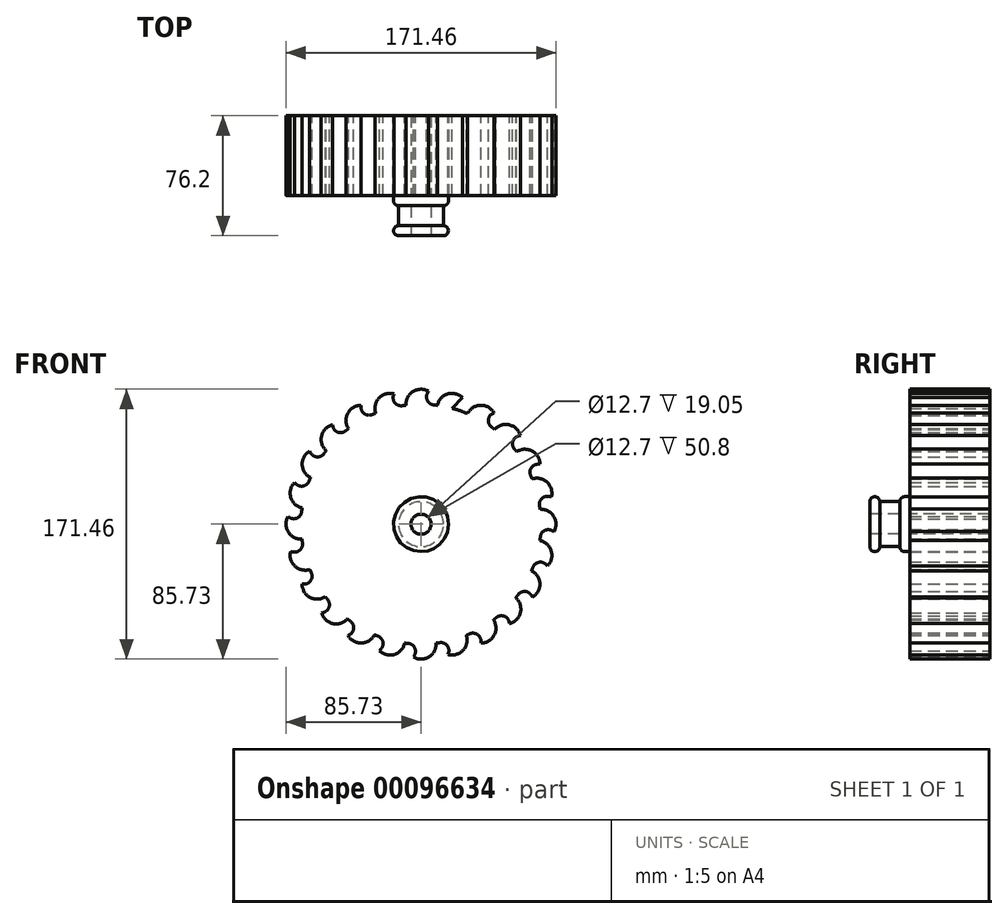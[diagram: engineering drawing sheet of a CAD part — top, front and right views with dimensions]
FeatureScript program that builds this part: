
annotation { "Feature Type Name" : "Feature", "Feature Type Description" : "" }
export const myFeature = defineFeature(function(context is Context, id is Id, definition is map)
    precondition{}
    {
        {
            var Q0;
            Q0=qCreatedBy(makeId("Front.planeOp"),FACE);
            var sketch = newSketch(context, id + "F0", { "sketchPlane" : qUnion([Q0])});
            skArc(sketch, "E0", {"start": v(-9.5, 75.6) * mm, "mid": v(-14.65, 74.78) * mm, "end": v(-19.72, 73.6) * mm});
            skLineSegment(sketch, "E1", {"start": v(0, 76.2) * mm, "end": v(0, 0) * mm, "construction": true});
            skArc(sketch, "E2", {"start": v(4.76, 84.45) * mm, "mid": v(-5.02, 84.3) * mm, "end": v(-9.5, 75.6) * mm});
            skLineSegment(sketch, "E3", {"start": v(0, 76.2) * mm, "end": v(4.76, 84.45) * mm});
            skLineSegment(sketch, "E4", {"start": v(0, 0) * mm, "end": v(82.95, 0) * mm, "construction": true});
            skArc(sketch, "E5.1.0", {"start": v(-17.26, 82.8) * mm, "mid": v(-26.66, 80.12) * mm, "end": v(-28.75, 70.57) * mm});
            skArc(sketch, "E5.2.0", {"start": v(-38.1, 75.52) * mm, "mid": v(-46.5, 70.5) * mm, "end": v(-46.04, 60.72) * mm});
            skArc(sketch, "E5.3.0", {"start": v(-56.35, 63.08) * mm, "mid": v(-63.15, 56.06) * mm, "end": v(-60.18, 46.74) * mm});
            skArc(sketch, "E5.4.0", {"start": v(-70.75, 46.35) * mm, "mid": v(-75.51, 37.8) * mm, "end": v(-70.23, 29.57) * mm});
            skArc(sketch, "E5.5.0", {"start": v(-80.34, 26.46) * mm, "mid": v(-82.72, 16.97) * mm, "end": v(-75.49, 10.39) * mm});
            skArc(sketch, "E5.6.0", {"start": v(-84.45, 4.76) * mm, "mid": v(-84.3, -5.02) * mm, "end": v(-75.6, -9.5) * mm});
            skArc(sketch, "E5.7.0", {"start": v(-82.8, -17.26) * mm, "mid": v(-80.12, -26.66) * mm, "end": v(-70.57, -28.75) * mm});
            skArc(sketch, "E5.8.0", {"start": v(-75.52, -38.1) * mm, "mid": v(-70.5, -46.5) * mm, "end": v(-60.72, -46.04) * mm});
            skArc(sketch, "E5.9.0", {"start": v(-63.08, -56.35) * mm, "mid": v(-56.06, -63.15) * mm, "end": v(-46.74, -60.18) * mm});
            skArc(sketch, "E5.10.0", {"start": v(-46.35, -70.75) * mm, "mid": v(-37.8, -75.51) * mm, "end": v(-29.57, -70.23) * mm});
            skArc(sketch, "E5.11.0", {"start": v(-26.46, -80.34) * mm, "mid": v(-16.97, -82.72) * mm, "end": v(-10.39, -75.49) * mm});
            skArc(sketch, "E5.12.0", {"start": v(-4.76, -84.45) * mm, "mid": v(5.02, -84.3) * mm, "end": v(9.5, -75.6) * mm});
            skArc(sketch, "E5.13.0", {"start": v(17.26, -82.8) * mm, "mid": v(26.66, -80.12) * mm, "end": v(28.75, -70.57) * mm});
            skArc(sketch, "E5.14.0", {"start": v(38.1, -75.52) * mm, "mid": v(46.5, -70.5) * mm, "end": v(46.04, -60.72) * mm});
            skArc(sketch, "E5.15.0", {"start": v(56.35, -63.08) * mm, "mid": v(63.15, -56.06) * mm, "end": v(60.18, -46.74) * mm});
            skArc(sketch, "E5.16.0", {"start": v(70.75, -46.35) * mm, "mid": v(75.51, -37.8) * mm, "end": v(70.23, -29.57) * mm});
            skArc(sketch, "E5.17.0", {"start": v(80.34, -26.46) * mm, "mid": v(82.72, -16.97) * mm, "end": v(75.49, -10.39) * mm});
            skArc(sketch, "E5.18.0", {"start": v(84.45, -4.76) * mm, "mid": v(84.3, 5.02) * mm, "end": v(75.6, 9.5) * mm});
            skArc(sketch, "E5.19.0", {"start": v(82.8, 17.26) * mm, "mid": v(80.12, 26.66) * mm, "end": v(70.57, 28.75) * mm});
            skArc(sketch, "E5.20.0", {"start": v(75.52, 38.1) * mm, "mid": v(70.5, 46.5) * mm, "end": v(60.72, 46.04) * mm});
            skArc(sketch, "E5.21.0", {"start": v(63.08, 56.35) * mm, "mid": v(56.06, 63.15) * mm, "end": v(46.74, 60.18) * mm});
            skArc(sketch, "E5.22.0", {"start": v(46.35, 70.75) * mm, "mid": v(37.8, 75.51) * mm, "end": v(29.57, 70.23) * mm});
            skArc(sketch, "E5.23.0", {"start": v(26.46, 80.34) * mm, "mid": v(16.97, 82.72) * mm, "end": v(10.39, 75.49) * mm});
            skLineSegment(sketch, "E6.1.0", {"start": v(-19.72, 73.6) * mm, "end": v(-17.26, 82.8) * mm});
            skLineSegment(sketch, "E6.2.0", {"start": v(-38.1, 66) * mm, "end": v(-38.1, 75.52) * mm});
            skLineSegment(sketch, "E6.3.0", {"start": v(-53.88, 53.88) * mm, "end": v(-56.35, 63.08) * mm});
            skLineSegment(sketch, "E6.4.0", {"start": v(-66, 38.1) * mm, "end": v(-70.75, 46.35) * mm});
            skLineSegment(sketch, "E6.5.0", {"start": v(-73.6, 19.72) * mm, "end": v(-80.34, 26.46) * mm});
            skLineSegment(sketch, "E6.6.0", {"start": v(-76.2, 0) * mm, "end": v(-84.45, 4.76) * mm});
            skLineSegment(sketch, "E6.7.0", {"start": v(-73.6, -19.72) * mm, "end": v(-82.8, -17.26) * mm});
            skLineSegment(sketch, "E6.8.0", {"start": v(-66, -38.1) * mm, "end": v(-75.52, -38.1) * mm});
            skLineSegment(sketch, "E6.9.0", {"start": v(-53.88, -53.88) * mm, "end": v(-63.08, -56.35) * mm});
            skLineSegment(sketch, "E6.10.0", {"start": v(-38.1, -66) * mm, "end": v(-46.35, -70.75) * mm});
            skLineSegment(sketch, "E6.11.0", {"start": v(-19.72, -73.6) * mm, "end": v(-26.46, -80.34) * mm});
            skLineSegment(sketch, "E6.12.0", {"start": v(0, -76.2) * mm, "end": v(-4.76, -84.45) * mm});
            skLineSegment(sketch, "E6.13.0", {"start": v(19.72, -73.6) * mm, "end": v(17.26, -82.8) * mm});
            skLineSegment(sketch, "E6.14.0", {"start": v(38.1, -66) * mm, "end": v(38.1, -75.52) * mm});
            skLineSegment(sketch, "E6.15.0", {"start": v(53.88, -53.88) * mm, "end": v(56.35, -63.08) * mm});
            skLineSegment(sketch, "E6.16.0", {"start": v(66, -38.1) * mm, "end": v(70.75, -46.35) * mm});
            skLineSegment(sketch, "E6.17.0", {"start": v(73.6, -19.72) * mm, "end": v(80.34, -26.46) * mm});
            skLineSegment(sketch, "E6.18.0", {"start": v(76.2, 0) * mm, "end": v(84.45, -4.76) * mm});
            skLineSegment(sketch, "E6.19.0", {"start": v(73.6, 19.72) * mm, "end": v(82.8, 17.26) * mm});
            skLineSegment(sketch, "E6.20.0", {"start": v(66, 38.1) * mm, "end": v(75.52, 38.1) * mm});
            skLineSegment(sketch, "E6.21.0", {"start": v(53.88, 53.88) * mm, "end": v(63.08, 56.35) * mm});
            skLineSegment(sketch, "E6.22.0", {"start": v(38.1, 66) * mm, "end": v(46.35, 70.75) * mm});
            skLineSegment(sketch, "E6.23.0", {"start": v(19.72, 73.6) * mm, "end": v(26.46, 80.34) * mm});
            skArc(sketch, "E7.trimOffspring", {"start": v(-46.04, 60.72) * mm, "mid": v(-50.08, 57.44) * mm, "end": v(-53.88, 53.88) * mm});
            skArc(sketch, "E8.trimOffspring", {"start": v(-28.75, 70.57) * mm, "mid": v(-33.5, 68.44) * mm, "end": v(-38.1, 66) * mm});
            skArc(sketch, "E9.trimOffspring", {"start": v(-60.18, 46.74) * mm, "mid": v(-63.23, 42.52) * mm, "end": v(-66, 38.1) * mm});
            skArc(sketch, "E10.trimOffspring", {"start": v(10.39, 75.49) * mm, "mid": v(5.2, 76.02) * mm, "end": v(0, 76.2) * mm});
            skArc(sketch, "E11.trimOffspring", {"start": v(29.57, 70.23) * mm, "mid": v(24.7, 72.08) * mm, "end": v(19.72, 73.6) * mm});
            skArc(sketch, "E12.trimOffspring", {"start": v(46.74, 60.18) * mm, "mid": v(42.52, 63.23) * mm, "end": v(38.1, 66) * mm});
            skArc(sketch, "E13.trimOffspring", {"start": v(60.72, 46.04) * mm, "mid": v(57.44, 50.08) * mm, "end": v(53.88, 53.88) * mm});
            skArc(sketch, "E14.trimOffspring", {"start": v(70.57, 28.75) * mm, "mid": v(68.44, 33.5) * mm, "end": v(66, 38.1) * mm});
            skArc(sketch, "E15.trimOffspring", {"start": v(75.6, 9.5) * mm, "mid": v(74.78, 14.65) * mm, "end": v(73.6, 19.72) * mm});
            skArc(sketch, "E16.trimOffspring", {"start": v(75.49, -10.39) * mm, "mid": v(76.02, -5.2) * mm, "end": v(76.2, 0) * mm});
            skArc(sketch, "E17.trimOffspring", {"start": v(70.23, -29.57) * mm, "mid": v(72.08, -24.7) * mm, "end": v(73.6, -19.72) * mm});
            skArc(sketch, "E18.trimOffspring", {"start": v(60.18, -46.74) * mm, "mid": v(63.23, -42.52) * mm, "end": v(66, -38.1) * mm});
            skArc(sketch, "E19.trimOffspring", {"start": v(46.04, -60.72) * mm, "mid": v(50.08, -57.44) * mm, "end": v(53.88, -53.88) * mm});
            skArc(sketch, "E20.trimOffspring", {"start": v(28.75, -70.57) * mm, "mid": v(33.5, -68.44) * mm, "end": v(38.1, -66) * mm});
            skArc(sketch, "E21.trimOffspring", {"start": v(9.5, -75.6) * mm, "mid": v(14.65, -74.78) * mm, "end": v(19.72, -73.6) * mm});
            skArc(sketch, "E22.trimOffspring", {"start": v(-10.39, -75.49) * mm, "mid": v(-5.2, -76.02) * mm, "end": v(0, -76.2) * mm});
            skArc(sketch, "E23.trimOffspring", {"start": v(-29.57, -70.23) * mm, "mid": v(-24.7, -72.08) * mm, "end": v(-19.72, -73.6) * mm});
            skArc(sketch, "E24.trimOffspring", {"start": v(-46.74, -60.18) * mm, "mid": v(-42.52, -63.23) * mm, "end": v(-38.1, -66) * mm});
            skArc(sketch, "E25.trimOffspring", {"start": v(-60.72, -46.04) * mm, "mid": v(-57.44, -50.08) * mm, "end": v(-53.88, -53.88) * mm});
            skArc(sketch, "E26.trimOffspring", {"start": v(-70.57, -28.75) * mm, "mid": v(-68.44, -33.5) * mm, "end": v(-66, -38.1) * mm});
            skArc(sketch, "E27.trimOffspring", {"start": v(-75.6, -9.5) * mm, "mid": v(-74.78, -14.65) * mm, "end": v(-73.6, -19.72) * mm});
            skArc(sketch, "E28.trimOffspring", {"start": v(-75.49, 10.39) * mm, "mid": v(-76.02, 5.2) * mm, "end": v(-76.2, 0) * mm});
            skArc(sketch, "E29.trimOffspring", {"start": v(-70.23, 29.57) * mm, "mid": v(-72.08, 24.7) * mm, "end": v(-73.6, 19.72) * mm});
            skSolve(sketch);
        }
        {
            var Q0;
            Q0=makeQuery(id+"F0.imprint","IMPRINT",FACE,{"disambiguationData":[TD([[makeQuery(id+"F0.imprint","IMPRINT",EDGE,{"derivedFrom":sQuery(id+"F0.wireOp",EDGE,"E0")}),1.0]])]});
            extrude(context, id + "F1", {"entities" : qUnion([Q0]), "depth" : 50.8 * mm});
        }
        {
            var Q0;
            Q0=makeQuery(id+"F1.opExtrude","CAP_FACE",FACE,{"disambiguationData":[OSD([sQuery(id+"F0.wireOp",EDGE,"E0"),sQuery(id+"F0.wireOp",EDGE,"E2"),sQuery(id+"F0.wireOp",EDGE,"E3"),sQuery(id+"F0.wireOp",EDGE,"E5.1.0"),sQuery(id+"F0.wireOp",EDGE,"E5.2.0"),sQuery(id+"F0.wireOp",EDGE,"E5.3.0"),sQuery(id+"F0.wireOp",EDGE,"E5.4.0"),sQuery(id+"F0.wireOp",EDGE,"E5.5.0"),sQuery(id+"F0.wireOp",EDGE,"E5.6.0"),sQuery(id+"F0.wireOp",EDGE,"E5.7.0"),sQuery(id+"F0.wireOp",EDGE,"E5.8.0"),sQuery(id+"F0.wireOp",EDGE,"E5.9.0"),sQuery(id+"F0.wireOp",EDGE,"E5.10.0"),sQuery(id+"F0.wireOp",EDGE,"E5.11.0"),sQuery(id+"F0.wireOp",EDGE,"E5.12.0"),sQuery(id+"F0.wireOp",EDGE,"E5.13.0"),sQuery(id+"F0.wireOp",EDGE,"E5.14.0"),sQuery(id+"F0.wireOp",EDGE,"E5.15.0"),sQuery(id+"F0.wireOp",EDGE,"E5.16.0"),sQuery(id+"F0.wireOp",EDGE,"E5.17.0"),sQuery(id+"F0.wireOp",EDGE,"E5.18.0"),sQuery(id+"F0.wireOp",EDGE,"E5.19.0"),sQuery(id+"F0.wireOp",EDGE,"E5.20.0"),sQuery(id+"F0.wireOp",EDGE,"E5.21.0"),sQuery(id+"F0.wireOp",EDGE,"E5.22.0"),sQuery(id+"F0.wireOp",EDGE,"E5.23.0"),sQuery(id+"F0.wireOp",EDGE,"E6.1.0"),sQuery(id+"F0.wireOp",EDGE,"E6.2.0"),sQuery(id+"F0.wireOp",EDGE,"E6.3.0"),sQuery(id+"F0.wireOp",EDGE,"E6.4.0"),sQuery(id+"F0.wireOp",EDGE,"E6.5.0"),sQuery(id+"F0.wireOp",EDGE,"E6.6.0"),sQuery(id+"F0.wireOp",EDGE,"E6.7.0"),sQuery(id+"F0.wireOp",EDGE,"E6.8.0"),sQuery(id+"F0.wireOp",EDGE,"E6.9.0"),sQuery(id+"F0.wireOp",EDGE,"E6.10.0"),sQuery(id+"F0.wireOp",EDGE,"E6.11.0"),sQuery(id+"F0.wireOp",EDGE,"E6.12.0"),sQuery(id+"F0.wireOp",EDGE,"E6.13.0"),sQuery(id+"F0.wireOp",EDGE,"E6.14.0"),sQuery(id+"F0.wireOp",EDGE,"E6.15.0"),sQuery(id+"F0.wireOp",EDGE,"E6.16.0"),sQuery(id+"F0.wireOp",EDGE,"E6.17.0"),sQuery(id+"F0.wireOp",EDGE,"E6.18.0"),sQuery(id+"F0.wireOp",EDGE,"E6.19.0"),sQuery(id+"F0.wireOp",EDGE,"E6.20.0"),sQuery(id+"F0.wireOp",EDGE,"E6.21.0"),sQuery(id+"F0.wireOp",EDGE,"E6.22.0"),sQuery(id+"F0.wireOp",EDGE,"E6.23.0"),sQuery(id+"F0.wireOp",EDGE,"E7.trimOffspring"),sQuery(id+"F0.wireOp",EDGE,"E8.trimOffspring"),sQuery(id+"F0.wireOp",EDGE,"E9.trimOffspring"),sQuery(id+"F0.wireOp",EDGE,"E10.trimOffspring"),sQuery(id+"F0.wireOp",EDGE,"E11.trimOffspring"),sQuery(id+"F0.wireOp",EDGE,"E12.trimOffspring"),sQuery(id+"F0.wireOp",EDGE,"E13.trimOffspring"),sQuery(id+"F0.wireOp",EDGE,"E14.trimOffspring"),sQuery(id+"F0.wireOp",EDGE,"E15.trimOffspring"),sQuery(id+"F0.wireOp",EDGE,"E16.trimOffspring"),sQuery(id+"F0.wireOp",EDGE,"E17.trimOffspring"),sQuery(id+"F0.wireOp",EDGE,"E18.trimOffspring"),sQuery(id+"F0.wireOp",EDGE,"E19.trimOffspring"),sQuery(id+"F0.wireOp",EDGE,"E20.trimOffspring"),sQuery(id+"F0.wireOp",EDGE,"E21.trimOffspring"),sQuery(id+"F0.wireOp",EDGE,"E22.trimOffspring"),sQuery(id+"F0.wireOp",EDGE,"E23.trimOffspring"),sQuery(id+"F0.wireOp",EDGE,"E24.trimOffspring"),sQuery(id+"F0.wireOp",EDGE,"E25.trimOffspring"),sQuery(id+"F0.wireOp",EDGE,"E26.trimOffspring"),sQuery(id+"F0.wireOp",EDGE,"E27.trimOffspring"),sQuery(id+"F0.wireOp",EDGE,"E28.trimOffspring"),sQuery(id+"F0.wireOp",EDGE,"E29.trimOffspring")])],"isStart":false});
            var sketch = newSketch(context, id + "F2", { "sketchPlane" : qUnion([Q0])});
            skPoint(sketch, "E30", {"position": v(0, 0) * mm});
            skSolve(sketch);
        }
        {
            var Q0;
            Q0=sQuery(id+"F2.wireOp",VERTEX,"E30");
            var Q1;
            Q1=makeQuery(id+"F1.opExtrude","SWEPT_BODY",BODY,{"disambiguationData":[OSD([sQuery(id+"F0.wireOp",EDGE,"E0"),sQuery(id+"F0.wireOp",EDGE,"E2"),sQuery(id+"F0.wireOp",EDGE,"E3"),sQuery(id+"F0.wireOp",EDGE,"E5.1.0"),sQuery(id+"F0.wireOp",EDGE,"E5.2.0"),sQuery(id+"F0.wireOp",EDGE,"E5.3.0"),sQuery(id+"F0.wireOp",EDGE,"E5.4.0"),sQuery(id+"F0.wireOp",EDGE,"E5.5.0"),sQuery(id+"F0.wireOp",EDGE,"E5.6.0"),sQuery(id+"F0.wireOp",EDGE,"E5.7.0"),sQuery(id+"F0.wireOp",EDGE,"E5.8.0"),sQuery(id+"F0.wireOp",EDGE,"E5.9.0"),sQuery(id+"F0.wireOp",EDGE,"E5.10.0"),sQuery(id+"F0.wireOp",EDGE,"E5.11.0"),sQuery(id+"F0.wireOp",EDGE,"E5.12.0"),sQuery(id+"F0.wireOp",EDGE,"E5.13.0"),sQuery(id+"F0.wireOp",EDGE,"E5.14.0"),sQuery(id+"F0.wireOp",EDGE,"E5.15.0"),sQuery(id+"F0.wireOp",EDGE,"E5.16.0"),sQuery(id+"F0.wireOp",EDGE,"E5.17.0"),sQuery(id+"F0.wireOp",EDGE,"E5.18.0"),sQuery(id+"F0.wireOp",EDGE,"E5.19.0"),sQuery(id+"F0.wireOp",EDGE,"E5.20.0"),sQuery(id+"F0.wireOp",EDGE,"E5.21.0"),sQuery(id+"F0.wireOp",EDGE,"E5.22.0"),sQuery(id+"F0.wireOp",EDGE,"E5.23.0"),sQuery(id+"F0.wireOp",EDGE,"E6.1.0"),sQuery(id+"F0.wireOp",EDGE,"E6.2.0"),sQuery(id+"F0.wireOp",EDGE,"E6.3.0"),sQuery(id+"F0.wireOp",EDGE,"E6.4.0"),sQuery(id+"F0.wireOp",EDGE,"E6.5.0"),sQuery(id+"F0.wireOp",EDGE,"E6.6.0"),sQuery(id+"F0.wireOp",EDGE,"E6.7.0"),sQuery(id+"F0.wireOp",EDGE,"E6.8.0"),sQuery(id+"F0.wireOp",EDGE,"E6.9.0"),sQuery(id+"F0.wireOp",EDGE,"E6.10.0"),sQuery(id+"F0.wireOp",EDGE,"E6.11.0"),sQuery(id+"F0.wireOp",EDGE,"E6.12.0"),sQuery(id+"F0.wireOp",EDGE,"E6.13.0"),sQuery(id+"F0.wireOp",EDGE,"E6.14.0"),sQuery(id+"F0.wireOp",EDGE,"E6.15.0"),sQuery(id+"F0.wireOp",EDGE,"E6.16.0"),sQuery(id+"F0.wireOp",EDGE,"E6.17.0"),sQuery(id+"F0.wireOp",EDGE,"E6.18.0"),sQuery(id+"F0.wireOp",EDGE,"E6.19.0"),sQuery(id+"F0.wireOp",EDGE,"E6.20.0"),sQuery(id+"F0.wireOp",EDGE,"E6.21.0"),sQuery(id+"F0.wireOp",EDGE,"E6.22.0"),sQuery(id+"F0.wireOp",EDGE,"E6.23.0"),sQuery(id+"F0.wireOp",EDGE,"E7.trimOffspring"),sQuery(id+"F0.wireOp",EDGE,"E8.trimOffspring"),sQuery(id+"F0.wireOp",EDGE,"E9.trimOffspring"),sQuery(id+"F0.wireOp",EDGE,"E10.trimOffspring"),sQuery(id+"F0.wireOp",EDGE,"E11.trimOffspring"),sQuery(id+"F0.wireOp",EDGE,"E12.trimOffspring"),sQuery(id+"F0.wireOp",EDGE,"E13.trimOffspring"),sQuery(id+"F0.wireOp",EDGE,"E14.trimOffspring"),sQuery(id+"F0.wireOp",EDGE,"E15.trimOffspring"),sQuery(id+"F0.wireOp",EDGE,"E16.trimOffspring"),sQuery(id+"F0.wireOp",EDGE,"E17.trimOffspring"),sQuery(id+"F0.wireOp",EDGE,"E18.trimOffspring"),sQuery(id+"F0.wireOp",EDGE,"E19.trimOffspring"),sQuery(id+"F0.wireOp",EDGE,"E20.trimOffspring"),sQuery(id+"F0.wireOp",EDGE,"E21.trimOffspring"),sQuery(id+"F0.wireOp",EDGE,"E22.trimOffspring"),sQuery(id+"F0.wireOp",EDGE,"E23.trimOffspring"),sQuery(id+"F0.wireOp",EDGE,"E24.trimOffspring"),sQuery(id+"F0.wireOp",EDGE,"E25.trimOffspring"),sQuery(id+"F0.wireOp",EDGE,"E26.trimOffspring"),sQuery(id+"F0.wireOp",EDGE,"E27.trimOffspring"),sQuery(id+"F0.wireOp",EDGE,"E28.trimOffspring"),sQuery(id+"F0.wireOp",EDGE,"E29.trimOffspring")])]});
            hole(context, id + "F3", {"style" : HoleStyle.SIMPLE, "endStyle" : HoleEndStyle.THROUGH, "holeDiameter" : 12.7 * mm, "locations" : qUnion([Q0]), "scope" : qUnion([Q1]), "isTappedThrough" : true});
        }
        {
            var Q0;
            Q0=makeQuery(id+"F1.opExtrude","CAP_FACE",FACE,{"disambiguationData":[OSD([sQuery(id+"F0.wireOp",EDGE,"E0"),sQuery(id+"F0.wireOp",EDGE,"E2"),sQuery(id+"F0.wireOp",EDGE,"E3"),sQuery(id+"F0.wireOp",EDGE,"E5.1.0"),sQuery(id+"F0.wireOp",EDGE,"E5.2.0"),sQuery(id+"F0.wireOp",EDGE,"E5.3.0"),sQuery(id+"F0.wireOp",EDGE,"E5.4.0"),sQuery(id+"F0.wireOp",EDGE,"E5.5.0"),sQuery(id+"F0.wireOp",EDGE,"E5.6.0"),sQuery(id+"F0.wireOp",EDGE,"E5.7.0"),sQuery(id+"F0.wireOp",EDGE,"E5.8.0"),sQuery(id+"F0.wireOp",EDGE,"E5.9.0"),sQuery(id+"F0.wireOp",EDGE,"E5.10.0"),sQuery(id+"F0.wireOp",EDGE,"E5.11.0"),sQuery(id+"F0.wireOp",EDGE,"E5.12.0"),sQuery(id+"F0.wireOp",EDGE,"E5.13.0"),sQuery(id+"F0.wireOp",EDGE,"E5.14.0"),sQuery(id+"F0.wireOp",EDGE,"E5.15.0"),sQuery(id+"F0.wireOp",EDGE,"E5.16.0"),sQuery(id+"F0.wireOp",EDGE,"E5.17.0"),sQuery(id+"F0.wireOp",EDGE,"E5.18.0"),sQuery(id+"F0.wireOp",EDGE,"E5.19.0"),sQuery(id+"F0.wireOp",EDGE,"E5.20.0"),sQuery(id+"F0.wireOp",EDGE,"E5.21.0"),sQuery(id+"F0.wireOp",EDGE,"E5.22.0"),sQuery(id+"F0.wireOp",EDGE,"E5.23.0"),sQuery(id+"F0.wireOp",EDGE,"E6.1.0"),sQuery(id+"F0.wireOp",EDGE,"E6.2.0"),sQuery(id+"F0.wireOp",EDGE,"E6.3.0"),sQuery(id+"F0.wireOp",EDGE,"E6.4.0"),sQuery(id+"F0.wireOp",EDGE,"E6.5.0"),sQuery(id+"F0.wireOp",EDGE,"E6.6.0"),sQuery(id+"F0.wireOp",EDGE,"E6.7.0"),sQuery(id+"F0.wireOp",EDGE,"E6.8.0"),sQuery(id+"F0.wireOp",EDGE,"E6.9.0"),sQuery(id+"F0.wireOp",EDGE,"E6.10.0"),sQuery(id+"F0.wireOp",EDGE,"E6.11.0"),sQuery(id+"F0.wireOp",EDGE,"E6.12.0"),sQuery(id+"F0.wireOp",EDGE,"E6.13.0"),sQuery(id+"F0.wireOp",EDGE,"E6.14.0"),sQuery(id+"F0.wireOp",EDGE,"E6.15.0"),sQuery(id+"F0.wireOp",EDGE,"E6.16.0"),sQuery(id+"F0.wireOp",EDGE,"E6.17.0"),sQuery(id+"F0.wireOp",EDGE,"E6.18.0"),sQuery(id+"F0.wireOp",EDGE,"E6.19.0"),sQuery(id+"F0.wireOp",EDGE,"E6.20.0"),sQuery(id+"F0.wireOp",EDGE,"E6.21.0"),sQuery(id+"F0.wireOp",EDGE,"E6.22.0"),sQuery(id+"F0.wireOp",EDGE,"E6.23.0"),sQuery(id+"F0.wireOp",EDGE,"E7.trimOffspring"),sQuery(id+"F0.wireOp",EDGE,"E8.trimOffspring"),sQuery(id+"F0.wireOp",EDGE,"E9.trimOffspring"),sQuery(id+"F0.wireOp",EDGE,"E10.trimOffspring"),sQuery(id+"F0.wireOp",EDGE,"E11.trimOffspring"),sQuery(id+"F0.wireOp",EDGE,"E12.trimOffspring"),sQuery(id+"F0.wireOp",EDGE,"E13.trimOffspring"),sQuery(id+"F0.wireOp",EDGE,"E14.trimOffspring"),sQuery(id+"F0.wireOp",EDGE,"E15.trimOffspring"),sQuery(id+"F0.wireOp",EDGE,"E16.trimOffspring"),sQuery(id+"F0.wireOp",EDGE,"E17.trimOffspring"),sQuery(id+"F0.wireOp",EDGE,"E18.trimOffspring"),sQuery(id+"F0.wireOp",EDGE,"E19.trimOffspring"),sQuery(id+"F0.wireOp",EDGE,"E20.trimOffspring"),sQuery(id+"F0.wireOp",EDGE,"E21.trimOffspring"),sQuery(id+"F0.wireOp",EDGE,"E22.trimOffspring"),sQuery(id+"F0.wireOp",EDGE,"E23.trimOffspring"),sQuery(id+"F0.wireOp",EDGE,"E24.trimOffspring"),sQuery(id+"F0.wireOp",EDGE,"E25.trimOffspring"),sQuery(id+"F0.wireOp",EDGE,"E26.trimOffspring"),sQuery(id+"F0.wireOp",EDGE,"E27.trimOffspring"),sQuery(id+"F0.wireOp",EDGE,"E28.trimOffspring"),sQuery(id+"F0.wireOp",EDGE,"E29.trimOffspring")])],"isStart":false});
            var sketch = newSketch(context, id + "F4", { "sketchPlane" : qUnion([Q0])});
            skCircle(sketch, "E31", {"center": v(0, 0) * mm, "radius": 14.29 * mm});
            skSolve(sketch);
        }
        {
            var Q0;
            Q0=makeQuery(id+"F4.imprint","IMPRINT",FACE,{"disambiguationData":[TD([[makeQuery(id+"F4.imprint","IMPRINT",EDGE,{"derivedFrom":sQuery(id+"F4.wireOp",EDGE,"E31")}),1.0]])]});
            extrude(context, id + "F5", {"entities" : qUnion([Q0]), "operationType" : NewBodyOperationType.ADD, "depth" : 25.4 * mm});
        }
        {
            var Q0;
            Q0=makeQuery(id+"F5.opExtrude","CAP_FACE",FACE,{"disambiguationData":[OSD([sQuery(id+"F3.hole-0.sketch.wireOp",EDGE,"core_line_2"),sQuery(id+"F3.hole-0.sketch.wireOp",EDGE,"core_line_3"),sQuery(id+"F4.wireOp",EDGE,"E31")])],"isStart":false});
            var sketch = newSketch(context, id + "F6", { "sketchPlane" : qUnion([Q0])});
            skCircle(sketch, "E32", {"center": v(0, 0) * mm, "radius": 17.46 * mm});
            skSolve(sketch);
        }
        {
            var Q0;
            Q0=makeQuery(id+"F6.imprint","IMPRINT",FACE,{"disambiguationData":[TD([[makeQuery(id+"F6.imprint","IMPRINT",EDGE,{"derivedFrom":sQuery(id+"F6.wireOp",EDGE,"E32")}),1.0]])]});
            extrude(context, id + "F7", {"entities" : qUnion([Q0]), "operationType" : NewBodyOperationType.ADD, "oppositeDirection" : true, "depth" : 6.35 * mm});
        }
        {
            var Q0;
            Q0=makeQuery(id+"F1.opExtrude","CAP_FACE",FACE,{"disambiguationData":[OSD([sQuery(id+"F0.wireOp",EDGE,"E0"),sQuery(id+"F0.wireOp",EDGE,"E2"),sQuery(id+"F0.wireOp",EDGE,"E3"),sQuery(id+"F0.wireOp",EDGE,"E5.1.0"),sQuery(id+"F0.wireOp",EDGE,"E5.2.0"),sQuery(id+"F0.wireOp",EDGE,"E5.3.0"),sQuery(id+"F0.wireOp",EDGE,"E5.4.0"),sQuery(id+"F0.wireOp",EDGE,"E5.5.0"),sQuery(id+"F0.wireOp",EDGE,"E5.6.0"),sQuery(id+"F0.wireOp",EDGE,"E5.7.0"),sQuery(id+"F0.wireOp",EDGE,"E5.8.0"),sQuery(id+"F0.wireOp",EDGE,"E5.9.0"),sQuery(id+"F0.wireOp",EDGE,"E5.10.0"),sQuery(id+"F0.wireOp",EDGE,"E5.11.0"),sQuery(id+"F0.wireOp",EDGE,"E5.12.0"),sQuery(id+"F0.wireOp",EDGE,"E5.13.0"),sQuery(id+"F0.wireOp",EDGE,"E5.14.0"),sQuery(id+"F0.wireOp",EDGE,"E5.15.0"),sQuery(id+"F0.wireOp",EDGE,"E5.16.0"),sQuery(id+"F0.wireOp",EDGE,"E5.17.0"),sQuery(id+"F0.wireOp",EDGE,"E5.18.0"),sQuery(id+"F0.wireOp",EDGE,"E5.19.0"),sQuery(id+"F0.wireOp",EDGE,"E5.20.0"),sQuery(id+"F0.wireOp",EDGE,"E5.21.0"),sQuery(id+"F0.wireOp",EDGE,"E5.22.0"),sQuery(id+"F0.wireOp",EDGE,"E5.23.0"),sQuery(id+"F0.wireOp",EDGE,"E6.1.0"),sQuery(id+"F0.wireOp",EDGE,"E6.2.0"),sQuery(id+"F0.wireOp",EDGE,"E6.3.0"),sQuery(id+"F0.wireOp",EDGE,"E6.4.0"),sQuery(id+"F0.wireOp",EDGE,"E6.5.0"),sQuery(id+"F0.wireOp",EDGE,"E6.6.0"),sQuery(id+"F0.wireOp",EDGE,"E6.7.0"),sQuery(id+"F0.wireOp",EDGE,"E6.8.0"),sQuery(id+"F0.wireOp",EDGE,"E6.9.0"),sQuery(id+"F0.wireOp",EDGE,"E6.10.0"),sQuery(id+"F0.wireOp",EDGE,"E6.11.0"),sQuery(id+"F0.wireOp",EDGE,"E6.12.0"),sQuery(id+"F0.wireOp",EDGE,"E6.13.0"),sQuery(id+"F0.wireOp",EDGE,"E6.14.0"),sQuery(id+"F0.wireOp",EDGE,"E6.15.0"),sQuery(id+"F0.wireOp",EDGE,"E6.16.0"),sQuery(id+"F0.wireOp",EDGE,"E6.17.0"),sQuery(id+"F0.wireOp",EDGE,"E6.18.0"),sQuery(id+"F0.wireOp",EDGE,"E6.19.0"),sQuery(id+"F0.wireOp",EDGE,"E6.20.0"),sQuery(id+"F0.wireOp",EDGE,"E6.21.0"),sQuery(id+"F0.wireOp",EDGE,"E6.22.0"),sQuery(id+"F0.wireOp",EDGE,"E6.23.0"),sQuery(id+"F0.wireOp",EDGE,"E7.trimOffspring"),sQuery(id+"F0.wireOp",EDGE,"E8.trimOffspring"),sQuery(id+"F0.wireOp",EDGE,"E9.trimOffspring"),sQuery(id+"F0.wireOp",EDGE,"E10.trimOffspring"),sQuery(id+"F0.wireOp",EDGE,"E11.trimOffspring"),sQuery(id+"F0.wireOp",EDGE,"E12.trimOffspring"),sQuery(id+"F0.wireOp",EDGE,"E13.trimOffspring"),sQuery(id+"F0.wireOp",EDGE,"E14.trimOffspring"),sQuery(id+"F0.wireOp",EDGE,"E15.trimOffspring"),sQuery(id+"F0.wireOp",EDGE,"E16.trimOffspring"),sQuery(id+"F0.wireOp",EDGE,"E17.trimOffspring"),sQuery(id+"F0.wireOp",EDGE,"E18.trimOffspring"),sQuery(id+"F0.wireOp",EDGE,"E19.trimOffspring"),sQuery(id+"F0.wireOp",EDGE,"E20.trimOffspring"),sQuery(id+"F0.wireOp",EDGE,"E21.trimOffspring"),sQuery(id+"F0.wireOp",EDGE,"E22.trimOffspring"),sQuery(id+"F0.wireOp",EDGE,"E23.trimOffspring"),sQuery(id+"F0.wireOp",EDGE,"E24.trimOffspring"),sQuery(id+"F0.wireOp",EDGE,"E25.trimOffspring"),sQuery(id+"F0.wireOp",EDGE,"E26.trimOffspring"),sQuery(id+"F0.wireOp",EDGE,"E27.trimOffspring"),sQuery(id+"F0.wireOp",EDGE,"E28.trimOffspring"),sQuery(id+"F0.wireOp",EDGE,"E29.trimOffspring")])],"isStart":false});
            var sketch = newSketch(context, id + "F8", { "sketchPlane" : qUnion([Q0])});
            skCircle(sketch, "E33.0", {"center": v(0, 0) * mm, "radius": 17.46 * mm});
            skSolve(sketch);
        }
        {
            var Q0;
            Q0 = qSketchRegion(id + "F8", true);
            extrude(context, id + "F9", {"entities" : qUnion([Q0]), "operationType" : NewBodyOperationType.ADD, "depth" : 6.35 * mm});
        }
        {
            var Q0;
            Q0=makeQuery(id+"F7.opExtrude","CAP_EDGE",EDGE,{"disambiguationData":[OSD([sQuery(id+"F6.wireOp",EDGE,"E32")])],"isStart":false});
            var Q1;
            Q1=makeQuery(id+"F9.opExtrude","CAP_EDGE",EDGE,{"disambiguationData":[OSD([sQuery(id+"F8.wireOp",EDGE,"E33.0")])],"isStart":false});
            var Q2;
            Q2=makeQuery(id+"F9.opExtrude","CAP_EDGE",EDGE,{"disambiguationData":[OSD([sQuery(id+"F8.wireOp",EDGE,"E33.0")])],"isStart":true});
            var Q3;
            Q3=makeQuery(id+"F7.opExtrude","CAP_EDGE",EDGE,{"disambiguationData":[OSD([sQuery(id+"F6.wireOp",EDGE,"E32")])],"isStart":true});
            fillet(context, id + "F10", {"entities" : qUnion([Q0, Q1, Q2, Q3]), "radius" : 3.17 * mm, "tangentPropagation" : true, "allowEdgeOverflow" : false});
        }
        {
            var Q0;
            Q0=makeQuery(id+"F1.opExtrude","SWEPT_EDGE",EDGE,{"disambiguationData":[OSD([sQuery(id+"F0.wireOp",EDGE,"E6.22.0"),sQuery(id+"F0.wireOp",EDGE,"E12.trimOffspring")])]});
            var Q1;
            Q1=makeQuery(id+"F1.opExtrude","SWEPT_EDGE",EDGE,{"disambiguationData":[OSD([sQuery(id+"F0.wireOp",EDGE,"E6.21.0"),sQuery(id+"F0.wireOp",EDGE,"E13.trimOffspring")])]});
            var Q2;
            Q2=makeQuery(id+"F1.opExtrude","SWEPT_EDGE",EDGE,{"disambiguationData":[OSD([sQuery(id+"F0.wireOp",EDGE,"E6.20.0"),sQuery(id+"F0.wireOp",EDGE,"E14.trimOffspring")])]});
            var Q3;
            Q3=makeQuery(id+"F1.opExtrude","SWEPT_EDGE",EDGE,{"disambiguationData":[OSD([sQuery(id+"F0.wireOp",EDGE,"E6.19.0"),sQuery(id+"F0.wireOp",EDGE,"E15.trimOffspring")])]});
            var Q4;
            Q4=makeQuery(id+"F1.opExtrude","SWEPT_EDGE",EDGE,{"disambiguationData":[OSD([sQuery(id+"F0.wireOp",EDGE,"E6.18.0"),sQuery(id+"F0.wireOp",EDGE,"E16.trimOffspring")])]});
            var Q5;
            Q5=makeQuery(id+"F1.opExtrude","SWEPT_EDGE",EDGE,{"disambiguationData":[OSD([sQuery(id+"F0.wireOp",EDGE,"E6.17.0"),sQuery(id+"F0.wireOp",EDGE,"E17.trimOffspring")])]});
            var Q6;
            Q6=makeQuery(id+"F1.opExtrude","SWEPT_EDGE",EDGE,{"disambiguationData":[OSD([sQuery(id+"F0.wireOp",EDGE,"E6.16.0"),sQuery(id+"F0.wireOp",EDGE,"E18.trimOffspring")])]});
            var Q7;
            Q7=makeQuery(id+"F1.opExtrude","SWEPT_EDGE",EDGE,{"disambiguationData":[OSD([sQuery(id+"F0.wireOp",EDGE,"E6.15.0"),sQuery(id+"F0.wireOp",EDGE,"E19.trimOffspring")])]});
            var Q8;
            Q8=makeQuery(id+"F1.opExtrude","SWEPT_EDGE",EDGE,{"disambiguationData":[OSD([sQuery(id+"F0.wireOp",EDGE,"E6.14.0"),sQuery(id+"F0.wireOp",EDGE,"E20.trimOffspring")])]});
            var Q9;
            Q9=makeQuery(id+"F1.opExtrude","SWEPT_EDGE",EDGE,{"disambiguationData":[OSD([sQuery(id+"F0.wireOp",EDGE,"E6.13.0"),sQuery(id+"F0.wireOp",EDGE,"E21.trimOffspring")])]});
            fillet(context, id + "F11", {"entities" : qUnion([Q0, Q1, Q2, Q3, Q4, Q5, Q6, Q7, Q8, Q9]), "radius" : 5.08 * mm, "tangentPropagation" : true, "allowEdgeOverflow" : false});
        }
        {
            var Q0;
            Q0=makeQuery(id+"F1.opExtrude","SWEPT_EDGE",EDGE,{"disambiguationData":[OSD([sQuery(id+"F0.wireOp",EDGE,"E6.12.0"),sQuery(id+"F0.wireOp",EDGE,"E22.trimOffspring")])]});
            var Q1;
            Q1=makeQuery(id+"F1.opExtrude","SWEPT_EDGE",EDGE,{"disambiguationData":[OSD([sQuery(id+"F0.wireOp",EDGE,"E6.11.0"),sQuery(id+"F0.wireOp",EDGE,"E23.trimOffspring")])]});
            var Q2;
            Q2=makeQuery(id+"F1.opExtrude","SWEPT_EDGE",EDGE,{"disambiguationData":[OSD([sQuery(id+"F0.wireOp",EDGE,"E6.10.0"),sQuery(id+"F0.wireOp",EDGE,"E24.trimOffspring")])]});
            var Q3;
            Q3=makeQuery(id+"F1.opExtrude","SWEPT_EDGE",EDGE,{"disambiguationData":[OSD([sQuery(id+"F0.wireOp",EDGE,"E6.9.0"),sQuery(id+"F0.wireOp",EDGE,"E25.trimOffspring")])]});
            var Q4;
            Q4=makeQuery(id+"F1.opExtrude","SWEPT_EDGE",EDGE,{"disambiguationData":[OSD([sQuery(id+"F0.wireOp",EDGE,"E3"),sQuery(id+"F0.wireOp",EDGE,"E10.trimOffspring")])]});
            var Q5;
            Q5=makeQuery(id+"F1.opExtrude","SWEPT_EDGE",EDGE,{"disambiguationData":[OSD([sQuery(id+"F0.wireOp",EDGE,"E0"),sQuery(id+"F0.wireOp",EDGE,"E6.1.0")])]});
            var Q6;
            Q6=makeQuery(id+"F1.opExtrude","SWEPT_EDGE",EDGE,{"disambiguationData":[OSD([sQuery(id+"F0.wireOp",EDGE,"E6.2.0"),sQuery(id+"F0.wireOp",EDGE,"E8.trimOffspring")])]});
            var Q7;
            Q7=makeQuery(id+"F1.opExtrude","SWEPT_EDGE",EDGE,{"disambiguationData":[OSD([sQuery(id+"F0.wireOp",EDGE,"E6.3.0"),sQuery(id+"F0.wireOp",EDGE,"E7.trimOffspring")])]});
            var Q8;
            Q8=makeQuery(id+"F1.opExtrude","SWEPT_EDGE",EDGE,{"disambiguationData":[OSD([sQuery(id+"F0.wireOp",EDGE,"E6.4.0"),sQuery(id+"F0.wireOp",EDGE,"E9.trimOffspring")])]});
            var Q9;
            Q9=makeQuery(id+"F1.opExtrude","SWEPT_EDGE",EDGE,{"disambiguationData":[OSD([sQuery(id+"F0.wireOp",EDGE,"E6.5.0"),sQuery(id+"F0.wireOp",EDGE,"E29.trimOffspring")])]});
            var Q10;
            Q10=makeQuery(id+"F1.opExtrude","SWEPT_EDGE",EDGE,{"disambiguationData":[OSD([sQuery(id+"F0.wireOp",EDGE,"E6.6.0"),sQuery(id+"F0.wireOp",EDGE,"E28.trimOffspring")])]});
            var Q11;
            Q11=makeQuery(id+"F1.opExtrude","SWEPT_EDGE",EDGE,{"disambiguationData":[OSD([sQuery(id+"F0.wireOp",EDGE,"E6.7.0"),sQuery(id+"F0.wireOp",EDGE,"E27.trimOffspring")])]});
            var Q12;
            Q12=makeQuery(id+"F1.opExtrude","SWEPT_EDGE",EDGE,{"disambiguationData":[OSD([sQuery(id+"F0.wireOp",EDGE,"E6.8.0"),sQuery(id+"F0.wireOp",EDGE,"E26.trimOffspring")])]});
            fillet(context, id + "F12", {"entities" : qUnion([Q0, Q1, Q2, Q3, Q4, Q5, Q6, Q7, Q8, Q9, Q10, Q11, Q12]), "radius" : 5.08 * mm, "tangentPropagation" : true, "allowEdgeOverflow" : false});
        }
    });
